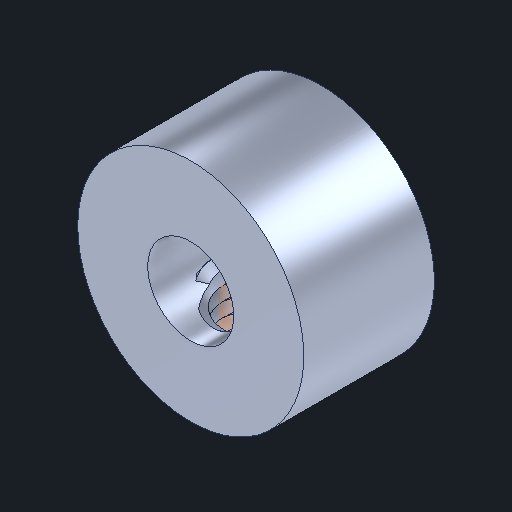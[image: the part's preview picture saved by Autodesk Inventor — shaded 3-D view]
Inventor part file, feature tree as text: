
AUTODESK INVENTOR PART (.ipt)
format: ipt  version: 2024 (Build 280153000, 153)  size: 589,824 bytes
history: native  units: in
note: dims shown in document units (in); Inventor stores cm internally (conversion verified against a paired STEP export)
features: other x6, sketch x3, plane x1
ambient origin geometry x8: Origin, YZ Plane, XZ Plane, XY Plane, X Axis, Y Axis, Z Axis, Center Point
bodies: Body1 (feature_tree), Body2 (feature_tree)
feature tree (10):
  other  "Shaft Collar Metal.ipt"
  other  "NONE::Shaft Collar Metal.ipt"
  other  "TaggingFeature1"
  sketch  "Sketch1"  dims[d0=0.3937in]
  sketch  "Sketch2"
  sketch  "Sketch3"
  plane  "Work Plane1"
  other  "Srf1"
  parser-record x1  (decoder bookkeeping rows leaked as tree rows — omitted from the tree; the rows remain in map.json)
  other  "Srf1::Derived"
